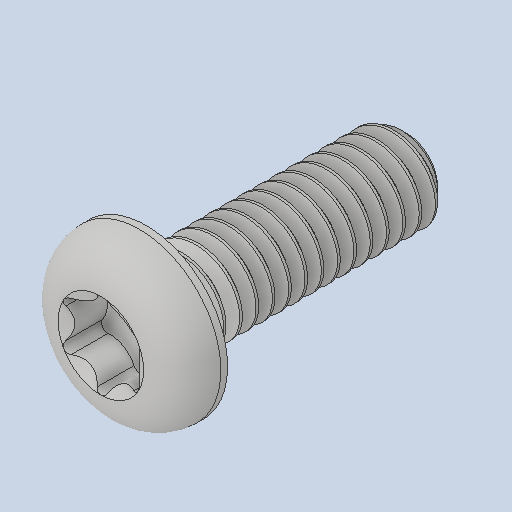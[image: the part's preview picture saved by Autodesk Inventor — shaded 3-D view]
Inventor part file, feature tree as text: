
AUTODESK INVENTOR PART (.ipt)
format: ipt  version: 2023.4 (Build 274418000, 418)  size: 657,408 bytes
history: native  units: in
note: dims shown in document units (in); Inventor stores cm internally (conversion verified against a paired STEP export)
features: extrude x1
ambient origin geometry x8: Origin, YZ Plane, XZ Plane, XY Plane, X Axis, Y Axis, Z Axis, Center Point
bodies: Solid1 (feature_tree)
feature tree (1):
  extrude  "Extrude16"  [1 undecoded]
note: 1 required parameter value undecoded (feature->parameter linkage not recoverable at this tier; creation-order binding heuristic only, values carry confidence <= 0.55)
